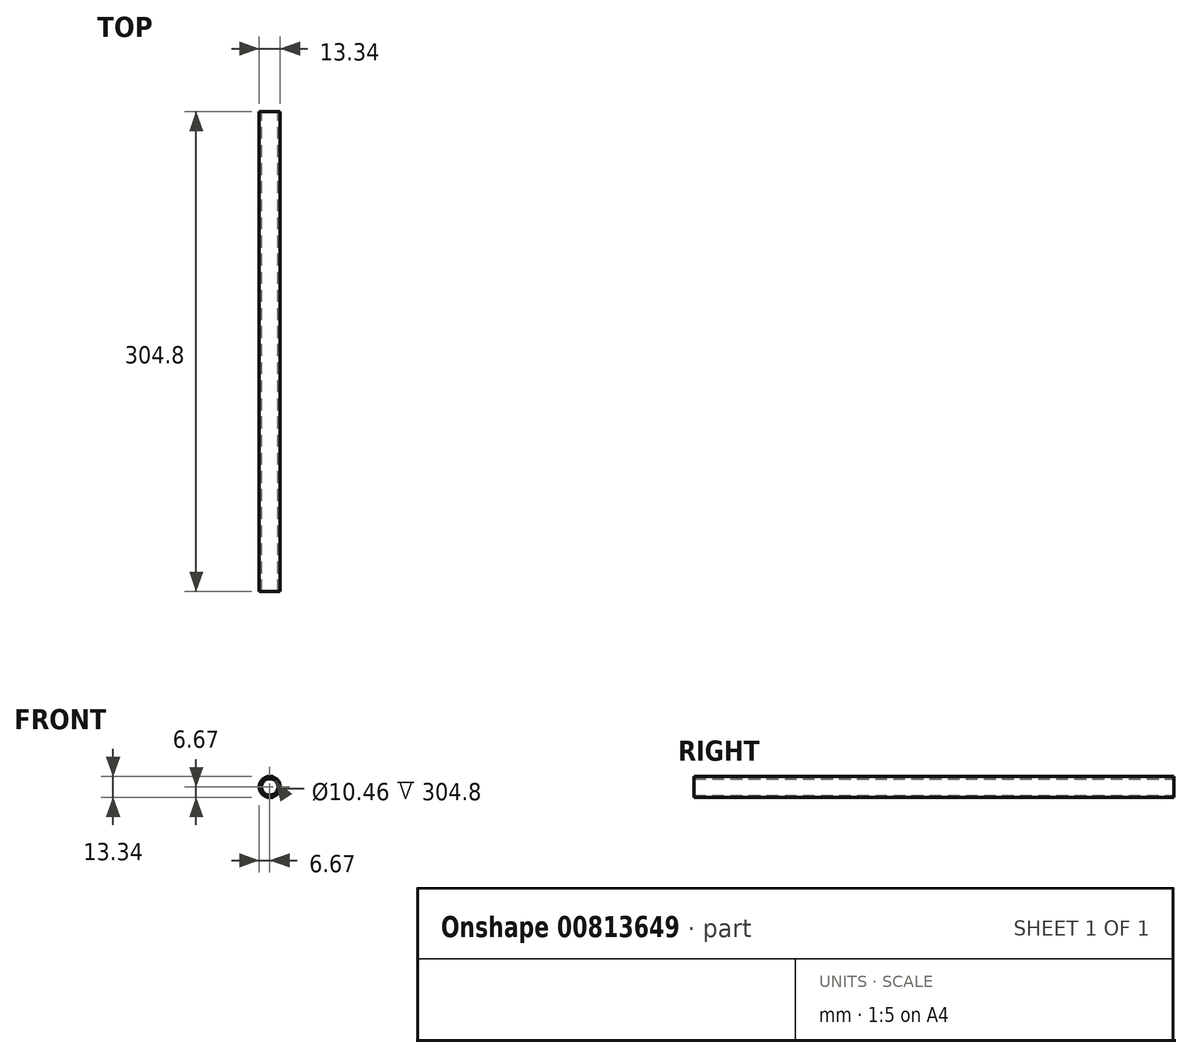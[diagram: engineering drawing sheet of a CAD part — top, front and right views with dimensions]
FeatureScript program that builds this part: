
annotation { "Feature Type Name" : "Feature", "Feature Type Description" : "" }
export const myFeature = defineFeature(function(context is Context, id is Id, definition is map)
    precondition{}
    {
        {
            var Q0;
            Q0=qCreatedBy(makeId("Front.planeOp"),FACE);
            var sketch = newSketch(context, id + "F0", { "sketchPlane" : qUnion([Q0])});
            skCircle(sketch, "E0", {"center": v(0, 0) * mm, "radius": 6.67 * mm});
            skCircle(sketch, "E1", {"center": v(0, 0) * mm, "radius": 5.23 * mm});
            skSolve(sketch);
        }
        {
            var Q0;
            Q0 = qSketchRegion(id + "F0", true);
            extrude(context, id + "F1", {"entities" : qUnion([Q0]), "endBound" : BoundingType.SYMMETRIC, "depth" : 304.8 * mm, "offsetDistance" : 25.4 * mm});
        }
    });
